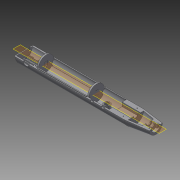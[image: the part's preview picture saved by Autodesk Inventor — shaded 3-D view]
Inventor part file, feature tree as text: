
AUTODESK INVENTOR PART (.ipt)
format: ipt  version: 2014 (Build 180170000, 170)  size: 555,520 bytes
history: native  units: mm
features: sketch x31, extrude x30, other x9, projected_geometry x3, fillet x2, loft x1
ambient origin geometry x8: Origin, YZ Plane, XZ Plane, XY Plane, X Axis, Y Axis, Z Axis, Center Point
bodies: Body1 (feature_tree)
feature tree (76):
  other  "Твердое тело1"
  extrude  "Выдавливание1"  Depth=11.0mm
  other  "РабПлоскость1"
  sketch  "Эскиз3"
  extrude  "Выдавливание2"  Depth=13.0mm
  loft  "Лофт2"
  extrude  "Выдавливание3"  Depth=180.0mm
  extrude  "Выдавливание4"  Depth=9.0mm
  extrude  "Выдавливание_Стойки"  Depth=6.0mm
  other  "РабПлоскость2"
  extrude  "Выдавливание Кнопки"  Depth=1.2mm TaperAngle=0.0deg
  fillet  "Сопряжение Торец копуса"  [1 undecoded]
  other  "РабПлоскость3"
  extrude  "Выдавливание7"  TaperAngle=0.0deg  [1 undecoded]
  extrude  "Выдавливание8"  Depth=1.5mm
  extrude  "Выдавливание9"  Depth=0.8mm
  other  "РабПлоскость4"
  extrude  "Выдавливание10"  Depth=1.0mm
  extrude  "Выдавливание11"  Depth=28.0mm TaperAngle=0.0deg
  other  "РабПлоскость5 Середина корпуса"
  extrude  "Выдавливание12"  Depth=4.0mm
  extrude  "Выдавливание13"  Depth=3.0mm
  extrude  "Выдавливание14"  Depth=2.0mm TaperAngle=0.0deg
  extrude  "Выдавливание15"  Depth=1.5mm
  extrude  "Выдавливание16"  Depth=4.0mm
  extrude  "Выдавливание17"  Depth=4.0mm
  extrude  "Выдавливание18"  Depth=25.0mm
  extrude  "Выдавливание19"  Depth=120.0mm
  extrude  "Выдавливание20"  Depth=1.0mm
  extrude  "Выдавливание21"  Depth=1.0mm
  other  "Выступ1"
  other  "Выступ2"
  extrude  "Выдавливание22"  Depth=11.0mm
  fillet  "Сопряжение4"  Radius=11.0mm
  extrude  "Выдавливание23"  Depth=4.0mm
  extrude  "Выдавливание24"  Depth=4.0mm
  extrude  "Выдавливание25"  Depth=15.0mm
  extrude  "Выдавливание26"  Depth=10.0mm TaperAngle=0.0deg
  extrude  "Выдавливание27"  Depth=2.0mm
  extrude  "Выдавливание28"  Depth=15.0mm
  extrude  "Выдавливание29"  Depth=2.0mm
  extrude  "Выдавливание30"  Depth=3.0mm
  sketch  "Эскиз1"
  sketch  "Эскиз4"
  other  "Ребра2"
  sketch  "Эскиз5"
  sketch  "Эскиз6"
  sketch  "Эскиз7"
  sketch  "Эскиз8"
  sketch  "Эскиз9"
  sketch  "Эскиз10"
  sketch  "Эскиз11"
  sketch  "Эскиз13"
  sketch  "Эскиз14"
  sketch  "Эскиз18"
  sketch  "Эскиз19"
  sketch  "Эскиз20"
  projected_geometry  "Спроецированная петля1"
  sketch  "Эскиз21"
  sketch  "Эскиз22"
  projected_geometry  "Спроецированная петля2"
  sketch  "Эскиз23"
  sketch  "Эскиз24"
  projected_geometry  "Спроецированная петля3"
  sketch  "Эскиз25"
  sketch  "Эскиз26"
  sketch  "Эскиз27"
  sketch  "Эскиз28"
  sketch  "Эскиз29"
  sketch  "Эскиз30"
  sketch  "Эскиз31"
  sketch  "Эскиз32"
  sketch  "Эскиз33"
  sketch  "Эскиз34"
  sketch  "Эскиз35"
  sketch  "Эскиз36"
note: 2 required parameter values undecoded (feature->parameter linkage not recoverable at this tier; creation-order binding heuristic only, values carry confidence <= 0.55)
